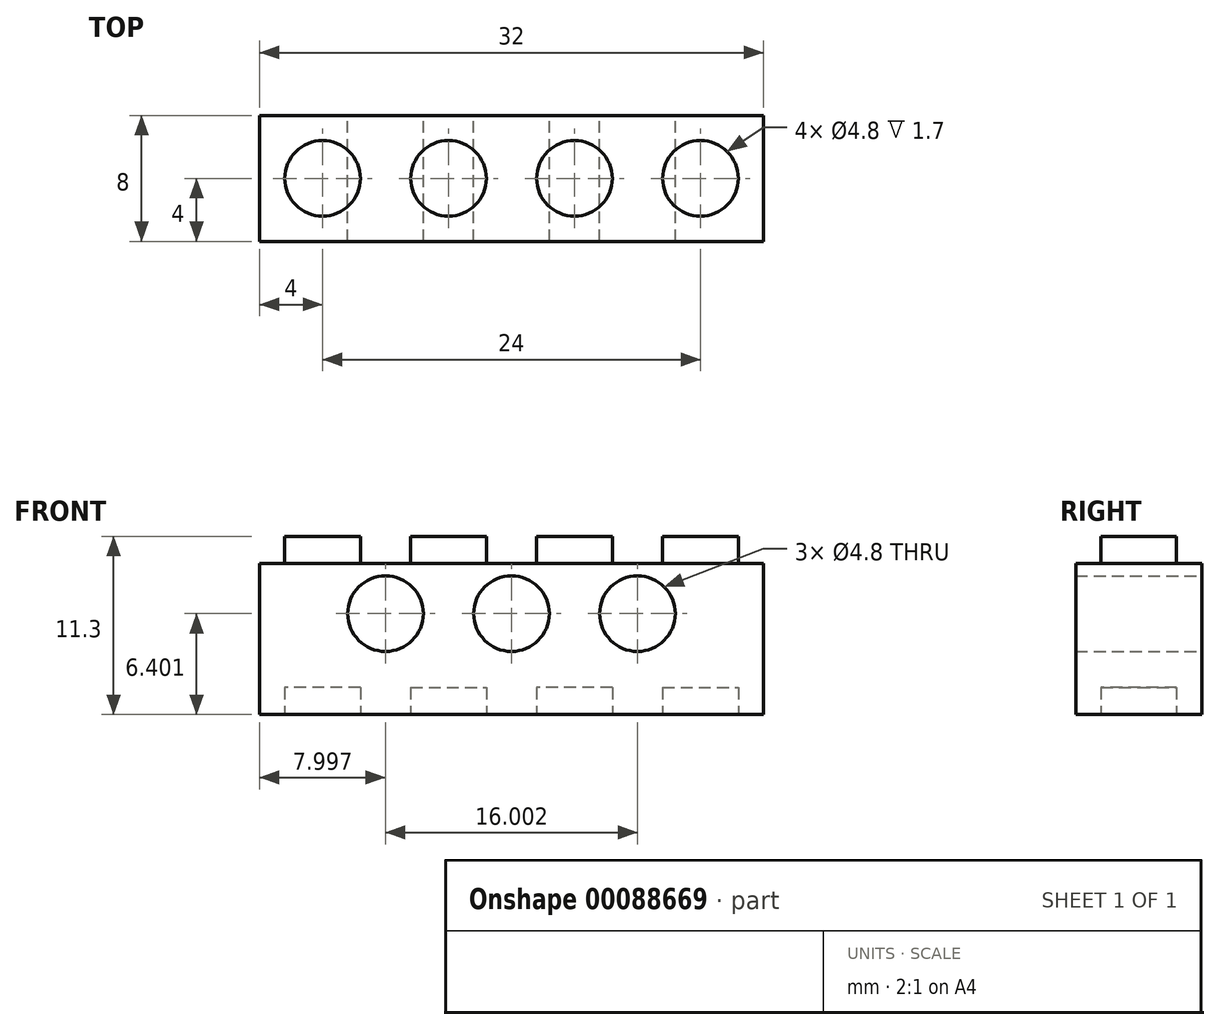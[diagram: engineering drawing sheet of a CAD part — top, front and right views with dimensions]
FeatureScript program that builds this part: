
annotation { "Feature Type Name" : "Feature", "Feature Type Description" : "" }
export const myFeature = defineFeature(function(context is Context, id is Id, definition is map)
    precondition{}
    {
        {
            var Q0;
            Q0=qCreatedBy(makeId("Front.planeOp"),FACE);
            var sketch = newSketch(context, id + "F0", { "sketchPlane" : qUnion([Q0])});
            skLineSegment(sketch, "E0.bottom", {"start": v(-4, 9.6) * mm, "end": v(-2.4, 9.6) * mm});
            skLineSegment(sketch, "E0.top", {"start": v(-4, 0) * mm, "end": v(4, 0) * mm});
            skLineSegment(sketch, "E0.left", {"start": v(-4, 9.6) * mm, "end": v(-4, 0) * mm});
            skLineSegment(sketch, "E0.right", {"start": v(4, 9.6) * mm, "end": v(4, 0) * mm});
            skLineSegment(sketch, "E1.top", {"start": v(-2.4, 11.3) * mm, "end": v(2.4, 11.3) * mm});
            skLineSegment(sketch, "E1.left", {"start": v(-2.4, 9.6) * mm, "end": v(-2.4, 11.3) * mm});
            skLineSegment(sketch, "E1.right", {"start": v(2.4, 9.6) * mm, "end": v(2.4, 11.3) * mm});
            skLineSegment(sketch, "E2", {"start": v(0, 0) * mm, "end": v(0, 24.04) * mm, "construction": true});
            skLineSegment(sketch, "E3.trimOffspring", {"start": v(2.4, 9.6) * mm, "end": v(4, 9.6) * mm});
            skSolve(sketch);
        }
        {
            var Q0;
            Q0=makeQuery(id+"F0.imprint","IMPRINT",FACE,{"disambiguationData":[TD([[makeQuery(id+"F0.imprint","IMPRINT",EDGE,{"derivedFrom":sQuery(id+"F0.wireOp",EDGE,"E0.bottom")}),-1.0]])]});
            extrude(context, id + "F1", {"entities" : qUnion([Q0]), "depth" : 8 * mm});
        }
        {
            var Q0;
            Q0=qCreatedBy(makeId("Top.planeOp"),FACE);
            var Q1;
            Q1=makeQuery(id+"F1.opExtrude","CAP_VERTEX",VERTEX,{"disambiguationData":[OSD([sQuery(id+"F0.wireOp",EDGE,"E1.top"),sQuery(id+"F0.wireOp",EDGE,"E1.right")])],"isStart":true});
            cPlane(context, id + "F2", {"entities" : qUnion([Q0, Q1]), "cplaneType" : CPlaneType.PLANE_POINT, "offset" : 152.4 * mm, "width" : 152.4 * mm, "height" : 152.4 * mm});
        }
        {
            var Q0;
            Q0=qCreatedBy(id+"F2.planeOp",FACE);
            var sketch = newSketch(context, id + "F3", { "sketchPlane" : qUnion([Q0])});
            skLineSegment(sketch, "E4.0", {"start": v(-4, -8) * mm, "end": v(-4, 0) * mm});
            skLineSegment(sketch, "E5.0", {"start": v(4, -8) * mm, "end": v(4, 0) * mm});
            skLineSegment(sketch, "E6", {"start": v(-4, 0) * mm, "end": v(4, 0) * mm});
            skLineSegment(sketch, "E7", {"start": v(-4, -8) * mm, "end": v(4, -8) * mm});
            skLineSegment(sketch, "E8", {"start": v(-4, 0) * mm, "end": v(4, -8) * mm, "construction": true});
            skLineSegment(sketch, "E9", {"start": v(-4, -8) * mm, "end": v(4, 0) * mm, "construction": true});
            skCircle(sketch, "E10", {"center": v(0, -4) * mm, "radius": 2.4 * mm});
            skSolve(sketch);
        }
        {
            var Q0;
            Q0=qSketchRegion(id+"F3",true);
            var Q1;
            Q1=makeQuery(id+"F1.opExtrude","SWEPT_FACE",FACE,{"disambiguationData":[OSD([sQuery(id+"F0.wireOp",EDGE,"E0.bottom")])]});
            extrude(context, id + "F4", {"entities" : qUnion([Q0]), "operationType" : NewBodyOperationType.REMOVE, "endBound" : BoundingType.UP_TO_SURFACE, "oppositeDirection" : true, "endBoundEntityFace" : qUnion([Q1]), "depth" : 25.4 * mm});
        }
        {
            var Q0;
            Q0=qCreatedBy(makeId("Top.planeOp"),FACE);
            var sketch = newSketch(context, id + "F5", { "sketchPlane" : qUnion([Q0])});
            skCircle(sketch, "E11.0", {"center": v(0, -4) * mm, "radius": 2.4 * mm});
            skSolve(sketch);
        }
        {
            var Q0;
            Q0=makeQuery(id+"F5.imprint","IMPRINT",FACE,{"disambiguationData":[TD([[makeQuery(id+"F5.imprint","IMPRINT",EDGE,{"derivedFrom":sQuery(id+"F5.wireOp",EDGE,"E11.0")}),1.0]])]});
            extrude(context, id + "F6", {"entities" : qUnion([Q0]), "operationType" : NewBodyOperationType.REMOVE, "depth" : 1.7 * mm});
        }
        {
            var Q0;
            Q0=qCreatedBy(makeId("Right.planeOp"),FACE);
            var Q1;
            Q1=makeQuery(id+"F1.opExtrude","CAP_VERTEX",VERTEX,{"disambiguationData":[OSD([sQuery(id+"F0.wireOp",EDGE,"E0.right"),sQuery(id+"F0.wireOp",EDGE,"E3.trimOffspring")])],"isStart":false});
            cPlane(context, id + "F7", {"entities" : qUnion([Q0, Q1]), "cplaneType" : CPlaneType.PLANE_POINT, "offset" : 152.4 * mm, "width" : 152.4 * mm, "height" : 152.4 * mm});
        }
        {
            var Q0;
            Q0=makeQuery(id+"F1.opExtrude","SWEPT_BODY",BODY,{"disambiguationData":[OSD([sQuery(id+"F0.wireOp",EDGE,"E0.bottom"),sQuery(id+"F0.wireOp",EDGE,"E0.top"),sQuery(id+"F0.wireOp",EDGE,"E0.left"),sQuery(id+"F0.wireOp",EDGE,"E0.right"),sQuery(id+"F0.wireOp",EDGE,"E1.top"),sQuery(id+"F0.wireOp",EDGE,"E1.left"),sQuery(id+"F0.wireOp",EDGE,"E1.right"),sQuery(id+"F0.wireOp",EDGE,"E3.trimOffspring")])]});
            var Q1;
            Q1=qCreatedBy(id+"F7.planeOp",FACE);
            mirror(context, id + "F8", {"operationType" : NewBodyOperationType.ADD, "entities" : qUnion([Q0]), "mirrorPlane" : qUnion([Q1])});
        }
        {
            var Q0;
            Q0=qCreatedBy(id+"F7.planeOp",FACE);
            var Q1;
            Q1=makeQuery(id+"F8.opPattern","COPY",VERTEX,{"derivedFrom":makeQuery(id+"F1.opExtrude","CAP_VERTEX",VERTEX,{"disambiguationData":[OSD([sQuery(id+"F0.wireOp",EDGE,"E0.bottom"),sQuery(id+"F0.wireOp",EDGE,"E0.left")])],"isStart":false}),"instanceName":"1"});
            cPlane(context, id + "F9", {"entities" : qUnion([Q0, Q1]), "cplaneType" : CPlaneType.PLANE_POINT, "offset" : 152.4 * mm, "width" : 152.4 * mm, "height" : 152.4 * mm});
        }
        {
            var Q0;
            Q0=makeQuery(id+"F1.opExtrude","SWEPT_BODY",BODY,{"disambiguationData":[OSD([sQuery(id+"F0.wireOp",EDGE,"E0.bottom"),sQuery(id+"F0.wireOp",EDGE,"E0.top"),sQuery(id+"F0.wireOp",EDGE,"E0.left"),sQuery(id+"F0.wireOp",EDGE,"E0.right"),sQuery(id+"F0.wireOp",EDGE,"E1.top"),sQuery(id+"F0.wireOp",EDGE,"E1.left"),sQuery(id+"F0.wireOp",EDGE,"E1.right"),sQuery(id+"F0.wireOp",EDGE,"E3.trimOffspring")])]});
            var Q1;
            Q1=qCreatedBy(id+"F9.planeOp",FACE);
            mirror(context, id + "F10", {"operationType" : NewBodyOperationType.ADD, "entities" : qUnion([Q0]), "mirrorPlane" : qUnion([Q1])});
        }
        {
            var Q0;
            Q0=qCreatedBy(makeId("Front.planeOp"),FACE);
            var sketch = newSketch(context, id + "F11", { "sketchPlane" : qUnion([Q0])});
            skLineSegment(sketch, "E12.0", {"start": v(-4, 9.6) * mm, "end": v(28, 9.6) * mm, "construction": true});
            skLineSegment(sketch, "E13.0", {"start": v(28, 9.6) * mm, "end": v(28, 0) * mm, "construction": true});
            skLineSegment(sketch, "E14.0", {"start": v(-4, 0) * mm, "end": v(28, 0) * mm, "construction": true});
            skLineSegment(sketch, "E15.0", {"start": v(-4, 9.6) * mm, "end": v(-4, 0) * mm, "construction": true});
            skCircle(sketch, "E16", {"center": v(20, 6.4) * mm, "radius": 2.4 * mm});
            skCircle(sketch, "E17", {"center": v(12, 6.4) * mm, "radius": 2.4 * mm});
            skCircle(sketch, "E18", {"center": v(4, 6.4) * mm, "radius": 2.4 * mm});
            skSolve(sketch);
        }
        {
            var Q0;
            Q0 = qSketchRegion(id + "F11", true);
            extrude(context, id + "F12", {"entities" : qUnion([Q0]), "operationType" : NewBodyOperationType.REMOVE, "depth" : 25.4 * mm});
        }
    });
